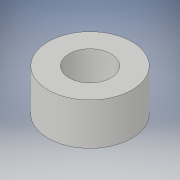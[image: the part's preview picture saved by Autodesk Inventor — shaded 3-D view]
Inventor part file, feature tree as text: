
AUTODESK INVENTOR PART (.ipt)
format: ipt  version: 2017 (Build 210142000, 142)  size: 95,232 bytes
history: native  units: in
note: dims shown in document units (in); Inventor stores cm internally (conversion verified against a paired STEP export)
features: extrude x1, sketch x1
ambient origin geometry x8: Origin, YZ Plane, XZ Plane, XY Plane, X Axis, Y Axis, Z Axis, Center Point
bodies: Solid1 (feature_tree)
feature tree (2):
  extrude  "Extrusion1"  Depth=0.25in
  sketch  "Sketch1"  dims[d0=0.25in d1=0.5in d2=0.25in d3=0.0in]
